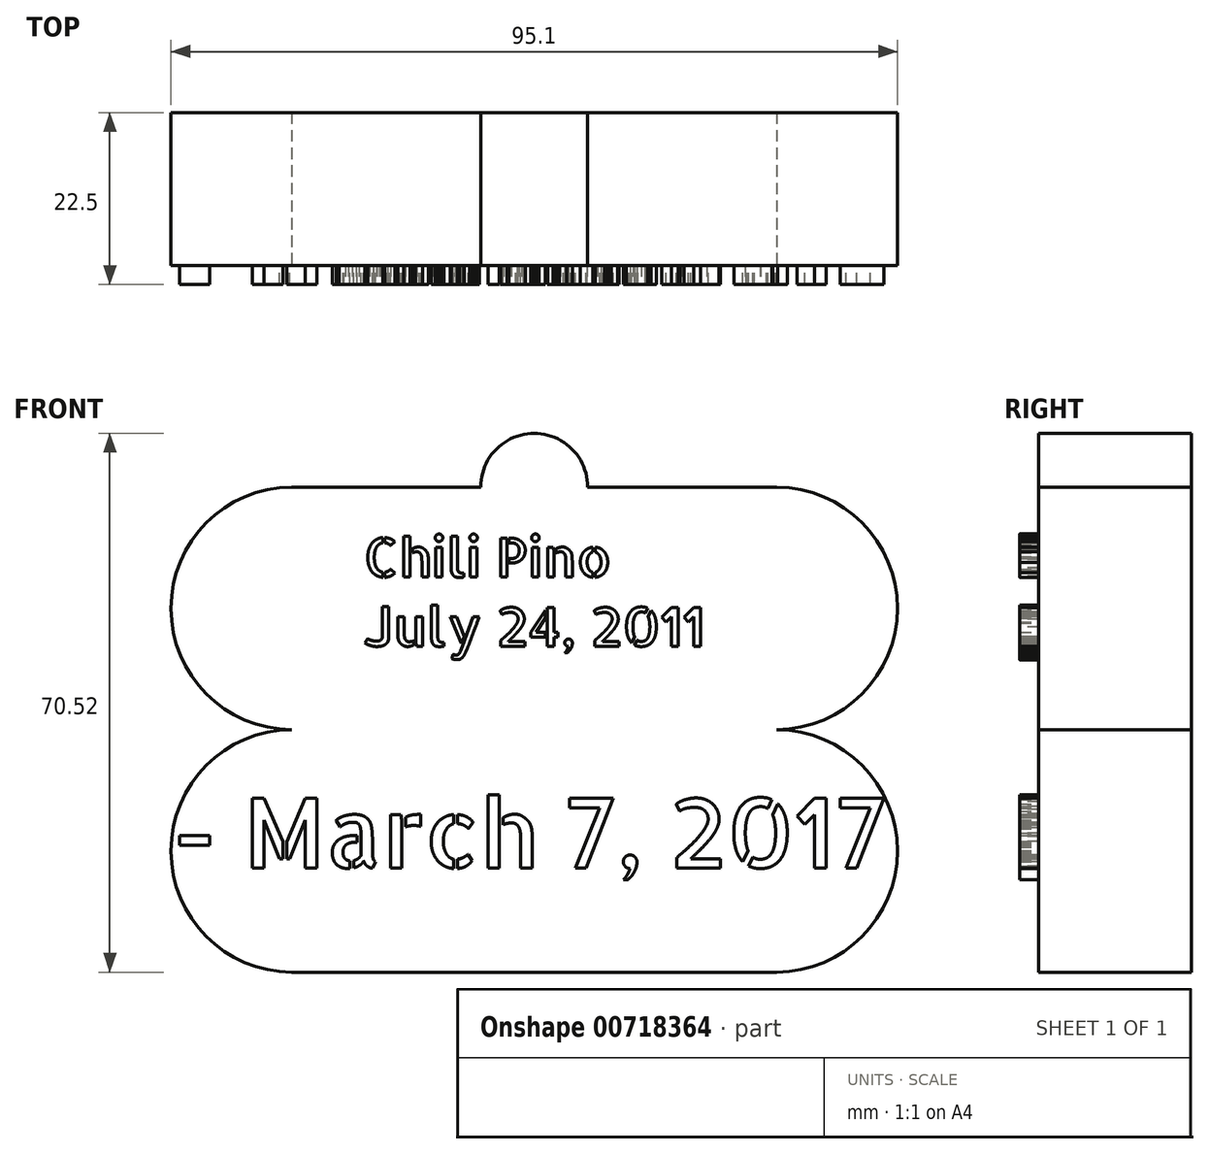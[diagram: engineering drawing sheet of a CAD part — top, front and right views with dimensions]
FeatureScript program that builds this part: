
annotation { "Feature Type Name" : "Feature", "Feature Type Description" : "" }
export const myFeature = defineFeature(function(context is Context, id is Id, definition is map)
    precondition{}
    {
        {
            var Q0;
            Q0=qCreatedBy(makeId("Front.planeOp"),FACE);
            var sketch = newSketch(context, id + "F0", { "sketchPlane" : qUnion([Q0])});
            skLineSegment(sketch, "E0.bottom", {"start": v(-62.2, 57.83) * mm, "end": v(64.8, 57.83) * mm});
            skLineSegment(sketch, "E0.top", {"start": v(-62.2, -69.17) * mm, "end": v(64.8, -69.17) * mm});
            skLineSegment(sketch, "E0.left", {"start": v(-62.2, 57.83) * mm, "end": v(-62.2, -69.17) * mm});
            skLineSegment(sketch, "E0.right", {"start": v(64.8, 57.83) * mm, "end": v(64.8, -69.17) * mm});
            skSolve(sketch);
        }
        {
            var Q0;
            Q0=makeQuery(id+"F0.imprint","IMPRINT",FACE,{"disambiguationData":[TD([[makeQuery(id+"F0.imprint","IMPRINT",EDGE,{"derivedFrom":sQuery(id+"F0.wireOp",EDGE,"E0.bottom")}),-1.0]])]});
            extrude(context, id + "F1", {"entities" : qUnion([Q0]), "depth" : 127 * mm, "offsetDistance" : 25 * mm});
        }
        {
            var Q0;
            Q0=makeQuery(id+"F1.opExtrude","CAP_FACE",FACE,{"disambiguationData":[OSD([sQuery(id+"F0.wireOp",EDGE,"E0.bottom"),sQuery(id+"F0.wireOp",EDGE,"E0.top"),sQuery(id+"F0.wireOp",EDGE,"E0.left"),sQuery(id+"F0.wireOp",EDGE,"E0.right")])],"isStart":false});
            var sketch = newSketch(context, id + "F2", { "sketchPlane" : qUnion([Q0])});
            skArc(sketch, "E1", {"start": v(-30.45, -5.67) * mm, "mid": v(-46.25, -21.55) * mm, "end": v(-30.45, -37.42) * mm});
            skArc(sketch, "E2", {"start": v(-30.45, -37.42) * mm, "mid": v(-46.25, -53.3) * mm, "end": v(-30.45, -69.17) * mm});
            skArc(sketch, "E3", {"start": v(33.05, -37.42) * mm, "mid": v(48.85, -21.55) * mm, "end": v(33.05, -5.67) * mm});
            skArc(sketch, "E4", {"start": v(33.05, -69.17) * mm, "mid": v(48.85, -53.3) * mm, "end": v(33.05, -37.42) * mm});
            skLineSegment(sketch, "E5", {"start": v(-30.45, -69.17) * mm, "end": v(33.05, -69.17) * mm});
            skLineSegment(sketch, "E6", {"start": v(-30.45, -5.67) * mm, "end": v(-8.7, -5.67) * mm});
            skLineSegment(sketch, "E7", {"start": v(33.05, -5.67) * mm, "end": v(11.3, -5.67) * mm});
            skArc(sketch, "E8", {"start": v(11.3, -5.67) * mm, "mid": v(1.3, 4.5) * mm, "end": v(-8.7, -5.67) * mm});
            skSolve(sketch);
        }
        {
            var Q0;
            Q0=makeQuery(id+"F2.imprint","IMPRINT",FACE,{"disambiguationData":[TD([[makeQuery(id+"F2.imprint","IMPRINT",EDGE,{"derivedFrom":sQuery(id+"F2.wireOp",EDGE,"E1")}),-1.0]])]});
            extrude(context, id + "F3", {"entities" : qUnion([Q0]), "operationType" : NewBodyOperationType.REMOVE, "oppositeDirection" : true, "depth" : 127 * mm, "offsetDistance" : 25 * mm});
        }
        {
            var Q0;
            Q0=makeQuery(id+"F1.opExtrude","CAP_FACE",FACE,{"disambiguationData":[OSD([sQuery(id+"F0.wireOp",EDGE,"E0.bottom"),sQuery(id+"F0.wireOp",EDGE,"E0.top"),sQuery(id+"F0.wireOp",EDGE,"E0.left"),sQuery(id+"F0.wireOp",EDGE,"E0.right")])],"isStart":false});
            extrude(context, id + "F4", {"entities" : qUnion([Q0]), "operationType" : NewBodyOperationType.REMOVE, "oppositeDirection" : true, "depth" : 107 * mm, "offsetDistance" : 25 * mm});
        }
        {
            var Q0;
            Q0=makeQuery(id+"F4.boolean.opBoolean","COPY",FACE,{"derivedFrom":makeQuery(id+"F4.opExtrude","CAP_FACE",FACE,{"disambiguationData":[OSD([sQuery(id+"F0.wireOp",EDGE,"E0.bottom"),sQuery(id+"F0.wireOp",EDGE,"E0.top"),sQuery(id+"F0.wireOp",EDGE,"E0.left"),sQuery(id+"F0.wireOp",EDGE,"E0.right")])],"isStart":false})});
            var sketch = newSketch(context, id + "F5", { "sketchPlane" : qUnion([Q0])});
            skLineSegment(sketch, "E9", {"start": v(-8.7, -5.67) * mm, "end": v(11.3, -5.67) * mm});
            skLineSegment(sketch, "E10", {"start": v(11.3, -5.67) * mm, "end": v(8.3, -5.67) * mm});
            skLineSegment(sketch, "E11", {"start": v(-8.7, -5.67) * mm, "end": v(-5.7, -5.67) * mm});
            skArc(sketch, "E12", {"start": v(8.3, -5.67) * mm, "mid": v(1.3, 1.35) * mm, "end": v(-5.7, -5.67) * mm});
            skSolve(sketch);
        }
        {
            var Q0;
            Q0=makeQuery(id+"F5.imprint","IMPRINT",FACE,{"disambiguationData":[TD([[makeQuery(id+"F5.imprint","IMPRINT",EDGE,{"derivedFrom":sQuery(id+"F5.wireOp",EDGE,"E9")}),1.0]])]});
            extrude(context, id + "F6", {"entities" : qUnion([Q0]), "operationType" : NewBodyOperationType.REMOVE, "oppositeDirection" : true, "depth" : 25 * mm, "offsetDistance" : 25 * mm});
        }
        {
            var Q0;
            Q0=makeQuery(id+"F4.boolean.opBoolean","COPY",FACE,{"derivedFrom":makeQuery(id+"F4.opExtrude","CAP_FACE",FACE,{"disambiguationData":[OSD([sQuery(id+"F0.wireOp",EDGE,"E0.bottom"),sQuery(id+"F0.wireOp",EDGE,"E0.top"),sQuery(id+"F0.wireOp",EDGE,"E0.left"),sQuery(id+"F0.wireOp",EDGE,"E0.right")])],"isStart":false})});
            var sketch = newSketch(context, id + "F7", { "sketchPlane" : qUnion([Q0])});
            skText(sketch, "E13", { "text": "Chili Pino \nJuly 24, 2011", "fontName": "AllertaStencil-Regular.ttf"});
            skText(sketch, "E14", { "text": "- March 7, 2017", "fontName": "AllertaStencil-Regular.ttf"});
            const initialGuessF7  = {"E13": [-0.02103, -0.01746, 1, 0, 0.0051], "E14": [-0.04617, -0.05555, 1, 0, 0.00913]};
            skSetInitialGuess(sketch, initialGuessF7);
            skSolve(sketch);
        }
        {
            var Q0;
            Q0 = qSketchRegion(id + "F7", true);
            extrude(context, id + "F8", {"entities" : qUnion([Q0]), "operationType" : NewBodyOperationType.ADD, "depth" : 2.5 * mm, "offsetDistance" : 25 * mm});
        }
    });
